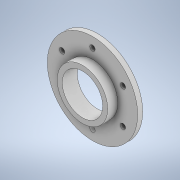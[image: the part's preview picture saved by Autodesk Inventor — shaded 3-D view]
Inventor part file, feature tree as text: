
AUTODESK INVENTOR PART (.ipt)
format: ipt  version: 2020 (Build 240168000, 168)  size: 136,704 bytes
history: native  units: in
note: dims shown in document units (in); Inventor stores cm internally (conversion verified against a paired STEP export)
features: extrude x2, sketch x2
ambient origin geometry x8: Origin, YZ Plane, XZ Plane, XY Plane, X Axis, Y Axis, Z Axis, Center Point
bodies: Solid1 (feature_tree)
feature tree (4):
  extrude  "Extrusion1"  Depth=1.75in
  extrude  "Extrusion2"  Depth=0.5in
  sketch  "Sketch1"  dims[d0=2.0157in d1=1.75in]
  sketch  "Sketch2"  dims[d2=0.2656in d3=4.5in d4=2.3622in d6=360.0deg d8=0.25in d9=0.0in d10=0.25in d11=0.5in d12=0.0in]
